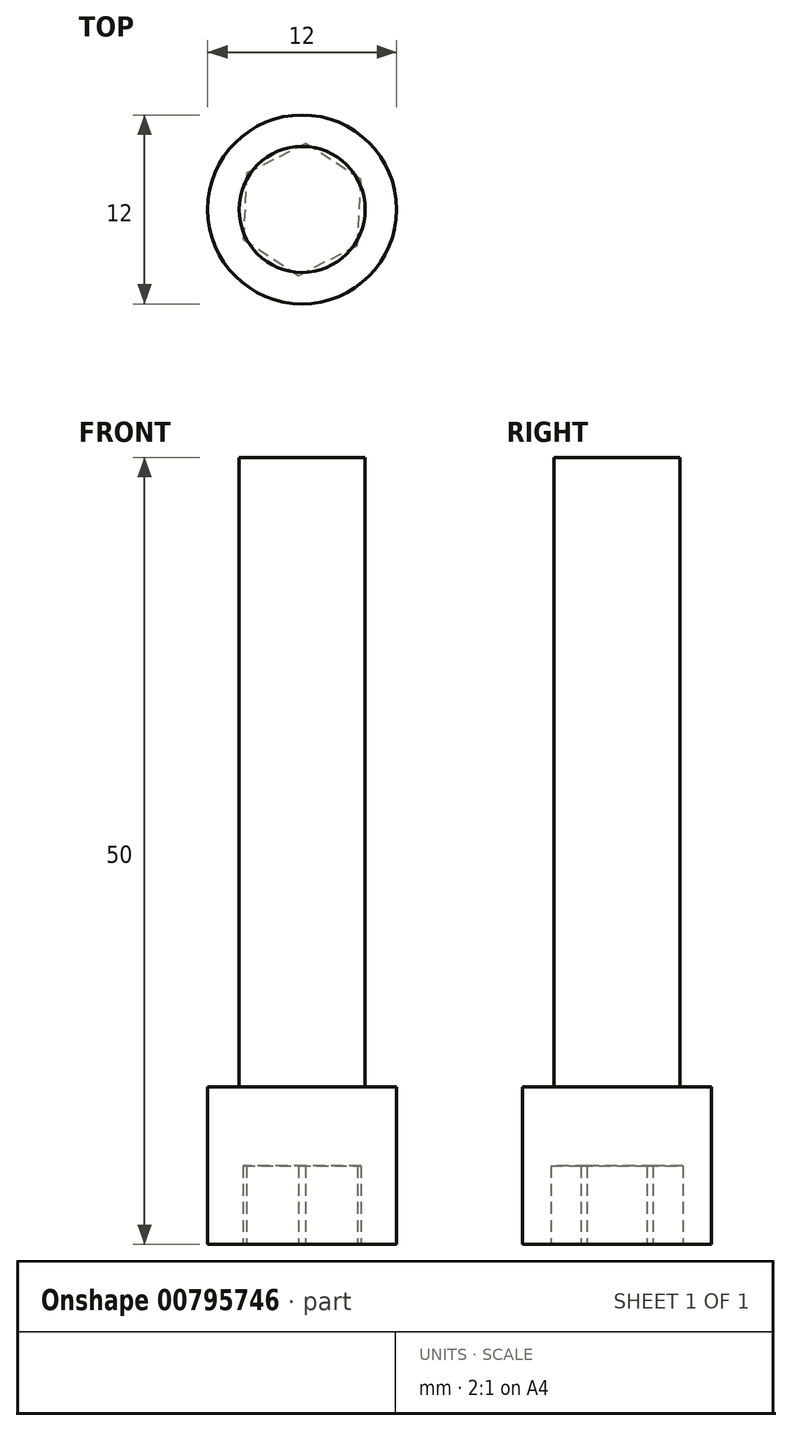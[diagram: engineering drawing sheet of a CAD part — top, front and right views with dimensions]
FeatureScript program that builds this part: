
annotation { "Feature Type Name" : "Feature", "Feature Type Description" : "" }
export const myFeature = defineFeature(function(context is Context, id is Id, definition is map)
    precondition{}
    {
        {
            var Q0;
            Q0=qCreatedBy(makeId("Top.planeOp"),FACE);
            var sketch = newSketch(context, id + "F0", { "sketchPlane" : qUnion([Q0])});
            skCircle(sketch, "E0", {"center": v(0, 0) * mm, "radius": 6 * mm});
            skSolve(sketch);
        }
        {
            var Q0;
            Q0 = qSketchRegion(id + "F0", true);
            extrude(context, id + "F1", {"entities" : qUnion([Q0]), "depth" : 10 * mm, "offsetDistance" : 25 * mm});
        }
        {
            var Q0;
            Q0=makeQuery(id+"F1.opExtrude","CAP_FACE",FACE,{"disambiguationData":[OSD([sQuery(id+"F0.wireOp",EDGE,"E0")])],"isStart":false});
            var sketch = newSketch(context, id + "F2", { "sketchPlane" : qUnion([Q0])});
            skCircle(sketch, "E1", {"center": v(0, 0) * mm, "radius": 4 * mm});
            skSolve(sketch);
        }
        {
            var Q0;
            Q0 = qSketchRegion(id + "F2", true);
            extrude(context, id + "F3", {"entities" : qUnion([Q0]), "operationType" : NewBodyOperationType.ADD, "depth" : 40 * mm, "offsetDistance" : 25 * mm});
        }
        {
            var Q0;
            Q0=makeQuery(id+"F1.opExtrude","CAP_FACE",FACE,{"disambiguationData":[OSD([sQuery(id+"F0.wireOp",EDGE,"E0")])],"isStart":true});
            var sketch = newSketch(context, id + "F4", { "sketchPlane" : qUnion([Q0])});
            skCircle(sketch, "E2.cCircle", {"center": v(0, 0) * mm, "radius": 3.64 * mm, "construction": true});
            skLineSegment(sketch, "E2.0", {"start": v(3.74, -1.9) * mm, "end": v(0.23, -4.2) * mm});
            skLineSegment(sketch, "E2.1", {"start": v(0.23, -4.2) * mm, "end": v(-3.52, -2.3) * mm});
            skLineSegment(sketch, "E2.2", {"start": v(-3.52, -2.3) * mm, "end": v(-3.74, 1.9) * mm});
            skLineSegment(sketch, "E2.3", {"start": v(-3.74, 1.9) * mm, "end": v(-0.23, 4.2) * mm});
            skLineSegment(sketch, "E2.4", {"start": v(-0.23, 4.2) * mm, "end": v(3.52, 2.3) * mm});
            skLineSegment(sketch, "E2.5", {"start": v(3.52, 2.3) * mm, "end": v(3.74, -1.9) * mm});
            skPoint(sketch, "E2.0.midPoint", {"position": v(1.98, -3.05) * mm});
            skSolve(sketch);
        }
        {
            var Q0;
            Q0=makeQuery(id+"F4.imprint","IMPRINT",FACE,{"disambiguationData":[TD([[makeQuery(id+"F4.imprint","IMPRINT",EDGE,{"derivedFrom":sQuery(id+"F4.wireOp",EDGE,"E2.0")}),-1.0]])]});
            extrude(context, id + "F5", {"entities" : qUnion([Q0]), "operationType" : NewBodyOperationType.REMOVE, "oppositeDirection" : true, "depth" : 5 * mm, "offsetDistance" : 25 * mm});
        }
    });
